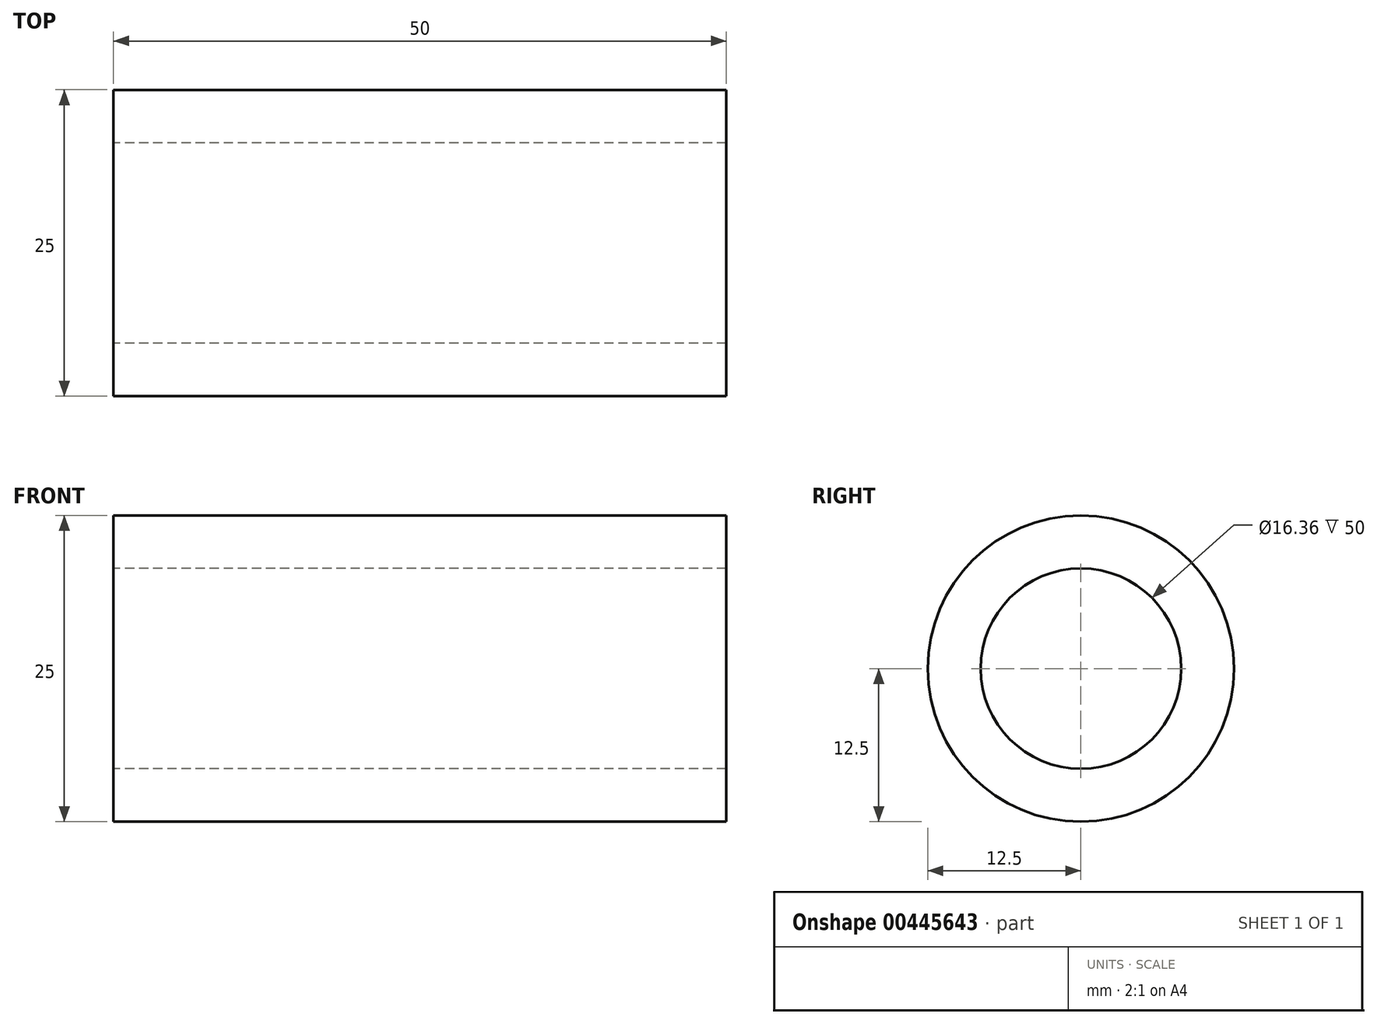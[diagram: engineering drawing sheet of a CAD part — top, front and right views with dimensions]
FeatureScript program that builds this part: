
annotation { "Feature Type Name" : "Feature", "Feature Type Description" : "" }
export const myFeature = defineFeature(function(context is Context, id is Id, definition is map)
    precondition{}
    {
        {
            var Q0;
            Q0=qCreatedBy(makeId("Right.planeOp"),FACE);
            var sketch = newSketch(context, id + "F0", { "sketchPlane" : qUnion([Q0])});
            skCircle(sketch, "E0", {"center": v(0, 0) * mm, "radius": 12.5 * mm});
            skCircle(sketch, "E1", {"center": v(0, 0) * mm, "radius": 8.18 * mm});
            skSolve(sketch);
        }
        {
            var Q0;
            Q0 = qSketchRegion(id + "F0", true);
            extrude(context, id + "F1", {"entities" : qUnion([Q0]), "depth" : 50 * mm});
        }
    });
